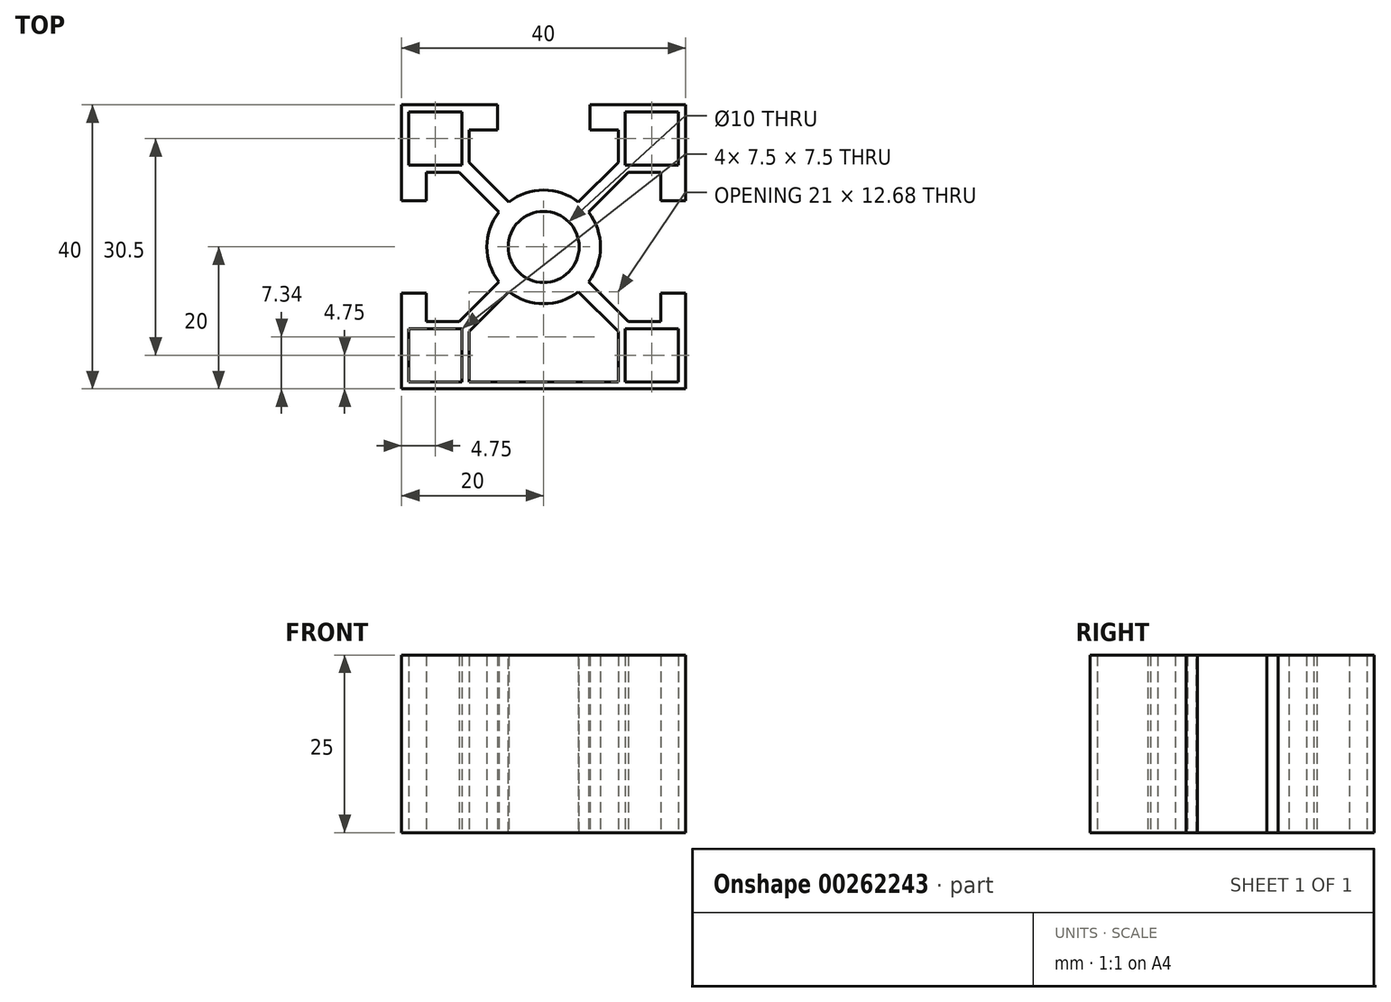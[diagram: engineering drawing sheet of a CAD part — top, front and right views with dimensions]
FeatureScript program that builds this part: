
annotation { "Feature Type Name" : "Feature", "Feature Type Description" : "" }
export const myFeature = defineFeature(function(context is Context, id is Id, definition is map)
    precondition{}
    {
        {
            var Q0;
            Q0=qCreatedBy(makeId("Top.planeOp"),FACE);
            var sketch = newSketch(context, id + "F0", { "sketchPlane" : qUnion([Q0])});
            skLineSegment(sketch, "E0.top", {"start": v(20, 20) * mm, "end": v(6.5, 20) * mm});
            skLineSegment(sketch, "E1.0", {"start": v(10.5, 16.5) * mm, "end": v(6.5, 16.5) * mm});
            skLineSegment(sketch, "E2.0", {"start": v(16.5, 6.5) * mm, "end": v(20, 6.5) * mm});
            skLineSegment(sketch, "E3", {"start": v(20, 20) * mm, "end": v(-20, -20) * mm, "construction": true});
            skLineSegment(sketch, "E4.MirrorCS", {"start": v(6.5, 16.5) * mm, "end": v(6.5, 20) * mm});
            skLineSegment(sketch, "E5.0", {"start": v(10.5, 11.91) * mm, "end": v(4.9, 6.32) * mm});
            skLineSegment(sketch, "E6.0", {"start": v(11.91, 10.5) * mm, "end": v(6.32, 4.9) * mm});
            skLineSegment(sketch, "E7.trimOffspring", {"start": v(20, 6.5) * mm, "end": v(20, 20) * mm});
            skLineSegment(sketch, "E8.trimOffspring", {"start": v(16.5, 6.5) * mm, "end": v(16.5, 10.5) * mm});
            skLineSegment(sketch, "E9", {"start": v(50.26, 0) * mm, "end": v(-51.39, 0) * mm, "construction": true});
            skLineSegment(sketch, "E10.0", {"start": v(10.5, 11.91) * mm, "end": v(10.5, 16.5) * mm});
            skLineSegment(sketch, "E10.1", {"start": v(11.91, 10.5) * mm, "end": v(16.5, 10.5) * mm});
            skLineSegment(sketch, "E11.0", {"start": v(19, 19) * mm, "end": v(11.5, 19) * mm});
            skLineSegment(sketch, "E11.1", {"start": v(19, 11.5) * mm, "end": v(19, 19) * mm});
            skLineSegment(sketch, "E12.0", {"start": v(11.5, 11.5) * mm, "end": v(19, 11.5) * mm});
            skLineSegment(sketch, "E12.1", {"start": v(11.5, 11.5) * mm, "end": v(11.5, 19) * mm});
            skArc(sketch, "E13", {"start": v(8, 0) * mm, "mid": v(7.57, 2.6) * mm, "end": v(6.32, 4.9) * mm});
            skLineSegment(sketch, "E14", {"start": v(0, 38.95) * mm, "end": v(0, -36.56) * mm, "construction": true});
            skArc(sketch, "E15.trimOffspring", {"start": v(4.9, 6.32) * mm, "mid": v(2.6, 7.57) * mm, "end": v(0, 8) * mm});
            skLineSegment(sketch, "E16.MirrorCS", {"start": v(-10.5, 16.5) * mm, "end": v(-6.5, 16.5) * mm});
            skArc(sketch, "E17.MirrorCS", {"start": v(-8, 0) * mm, "mid": v(-7.57, 2.6) * mm, "end": v(-6.32, 4.9) * mm});
            skLineSegment(sketch, "E18.MirrorCS", {"start": v(-11.5, 11.5) * mm, "end": v(-19, 11.5) * mm});
            skLineSegment(sketch, "E19.MirrorCS", {"start": v(-20, 20) * mm, "end": v(-6.5, 20) * mm});
            skLineSegment(sketch, "E20.MirrorCS", {"start": v(-19, 11.5) * mm, "end": v(-19, 19) * mm});
            skLineSegment(sketch, "E21.MirrorCS", {"start": v(-10.5, 11.91) * mm, "end": v(-10.5, 16.5) * mm});
            skLineSegment(sketch, "E22.MirrorCS", {"start": v(-10.5, 11.91) * mm, "end": v(-4.9, 6.32) * mm});
            skLineSegment(sketch, "E23.MirrorCS", {"start": v(-11.5, 11.5) * mm, "end": v(-11.5, 19) * mm});
            skLineSegment(sketch, "E24.MirrorCS", {"start": v(-16.5, 6.5) * mm, "end": v(-16.5, 10.5) * mm});
            skLineSegment(sketch, "E25.MirrorCS", {"start": v(-11.91, 10.5) * mm, "end": v(-16.5, 10.5) * mm});
            skLineSegment(sketch, "E26.MirrorCS", {"start": v(-19, 19) * mm, "end": v(-11.5, 19) * mm});
            skArc(sketch, "E27.MirrorCS", {"start": v(-4.9, 6.32) * mm, "mid": v(-2.6, 7.57) * mm, "end": v(0, 8) * mm});
            skLineSegment(sketch, "E28.MirrorCS", {"start": v(-6.5, 16.5) * mm, "end": v(-6.5, 20) * mm});
            skLineSegment(sketch, "E29.MirrorCS", {"start": v(-11.91, 10.5) * mm, "end": v(-6.32, 4.9) * mm});
            skLineSegment(sketch, "E30.MirrorCS", {"start": v(-20, 6.5) * mm, "end": v(-20, 20) * mm});
            skLineSegment(sketch, "E31.MirrorCS", {"start": v(-16.5, 6.5) * mm, "end": v(-20, 6.5) * mm});
            skLineSegment(sketch, "E32.MirrorCS", {"start": v(10.5, -11.91) * mm, "end": v(4.9, -6.32) * mm});
            skLineSegment(sketch, "E33.MirrorCS", {"start": v(10.5, -11.91) * mm, "end": v(10.5, -19) * mm});
            skLineSegment(sketch, "E34.MirrorCS", {"start": v(16.5, -6.5) * mm, "end": v(20, -6.5) * mm});
            skLineSegment(sketch, "E35.MirrorCS", {"start": v(-10.5, -11.91) * mm, "end": v(-4.9, -6.32) * mm});
            skLineSegment(sketch, "E36.MirrorCS", {"start": v(-11.91, -10.5) * mm, "end": v(-6.32, -4.9) * mm});
            skArc(sketch, "E37.MirrorCS", {"start": v(4.9, -6.32) * mm, "mid": v(2.6, -7.57) * mm, "end": v(0, -8) * mm});
            skArc(sketch, "E38.MirrorCS", {"start": v(8, 0) * mm, "mid": v(7.57, -2.6) * mm, "end": v(6.32, -4.9) * mm});
            skLineSegment(sketch, "E39.MirrorCS", {"start": v(-19, -19) * mm, "end": v(-11.5, -19) * mm});
            skLineSegment(sketch, "E40.MirrorCS", {"start": v(-20, -6.5) * mm, "end": v(-20, -20) * mm});
            skLineSegment(sketch, "E41.MirrorCS", {"start": v(-16.5, -6.5) * mm, "end": v(-20, -6.5) * mm});
            skArc(sketch, "E42.MirrorCS", {"start": v(-8, 0) * mm, "mid": v(-7.57, -2.6) * mm, "end": v(-6.32, -4.9) * mm});
            skLineSegment(sketch, "E43.MirrorCS", {"start": v(19, -19) * mm, "end": v(11.5, -19) * mm});
            skLineSegment(sketch, "E44.MirrorCS", {"start": v(11.5, -11.5) * mm, "end": v(11.5, -19) * mm});
            skLineSegment(sketch, "E45.MirrorCS", {"start": v(16.5, -6.5) * mm, "end": v(16.5, -10.5) * mm});
            skArc(sketch, "E46.MirrorCS", {"start": v(-4.9, -6.32) * mm, "mid": v(-2.6, -7.57) * mm, "end": v(0, -8) * mm});
            skLineSegment(sketch, "E47.MirrorCS", {"start": v(-16.5, -6.5) * mm, "end": v(-16.5, -10.5) * mm});
            skLineSegment(sketch, "E48.MirrorCS", {"start": v(-10.5, -11.91) * mm, "end": v(-10.5, -19) * mm});
            skLineSegment(sketch, "E49.MirrorCS", {"start": v(11.91, -10.5) * mm, "end": v(6.32, -4.9) * mm});
            skLineSegment(sketch, "E50.MirrorCS", {"start": v(19, -11.5) * mm, "end": v(19, -19) * mm});
            skLineSegment(sketch, "E51.MirrorCS", {"start": v(20, -6.5) * mm, "end": v(20, -20) * mm});
            skLineSegment(sketch, "E52.MirrorCS", {"start": v(-11.5, -11.5) * mm, "end": v(-19, -11.5) * mm});
            skLineSegment(sketch, "E53.MirrorCS", {"start": v(-20, -20) * mm, "end": v(20, -20) * mm});
            skLineSegment(sketch, "E54.MirrorCS", {"start": v(11.5, -11.5) * mm, "end": v(19, -11.5) * mm});
            skLineSegment(sketch, "E55.MirrorCS", {"start": v(-11.5, -11.5) * mm, "end": v(-11.5, -19) * mm});
            skLineSegment(sketch, "E56.MirrorCS", {"start": v(-11.91, -10.5) * mm, "end": v(-16.5, -10.5) * mm});
            skLineSegment(sketch, "E57.MirrorCS", {"start": v(11.91, -10.5) * mm, "end": v(16.5, -10.5) * mm});
            skLineSegment(sketch, "E58.MirrorCS", {"start": v(-19, -11.5) * mm, "end": v(-19, -19) * mm});
            skLineSegment(sketch, "E59", {"start": v(-10.5, -19) * mm, "end": v(10.5, -19) * mm});
            skSolve(sketch);
        }
        {
            var Q0;
            Q0=makeQuery(id+"F0.imprint","IMPRINT",FACE,{"disambiguationData":[TD([[makeQuery(id+"F0.imprint","IMPRINT",EDGE,{"derivedFrom":sQuery(id+"F0.wireOp",EDGE,"E0.top")}),1.0]])]});
            extrude(context, id + "F1", {"entities" : qUnion([Q0]), "depth" : 25 * mm});
        }
        {
            var Q0;
            Q0=makeQuery(id+"F1.opExtrude","CAP_FACE",FACE,{"disambiguationData":[OSD([sQuery(id+"F0.wireOp",EDGE,"E0.top"),sQuery(id+"F0.wireOp",EDGE,"E1.0"),sQuery(id+"F0.wireOp",EDGE,"E2.0"),sQuery(id+"F0.wireOp",EDGE,"E4.MirrorCS"),sQuery(id+"F0.wireOp",EDGE,"E5.0"),sQuery(id+"F0.wireOp",EDGE,"E6.0"),sQuery(id+"F0.wireOp",EDGE,"E7.trimOffspring"),sQuery(id+"F0.wireOp",EDGE,"E8.trimOffspring"),sQuery(id+"F0.wireOp",EDGE,"E10.0"),sQuery(id+"F0.wireOp",EDGE,"E10.1"),sQuery(id+"F0.wireOp",EDGE,"E11.0"),sQuery(id+"F0.wireOp",EDGE,"E11.1"),sQuery(id+"F0.wireOp",EDGE,"E12.0"),sQuery(id+"F0.wireOp",EDGE,"E12.1"),sQuery(id+"F0.wireOp",EDGE,"E13"),sQuery(id+"F0.wireOp",EDGE,"E15.trimOffspring"),sQuery(id+"F0.wireOp",EDGE,"E16.MirrorCS"),sQuery(id+"F0.wireOp",EDGE,"E17.MirrorCS"),sQuery(id+"F0.wireOp",EDGE,"E18.MirrorCS"),sQuery(id+"F0.wireOp",EDGE,"E20.MirrorCS"),sQuery(id+"F0.wireOp",EDGE,"E21.MirrorCS"),sQuery(id+"F0.wireOp",EDGE,"E22.MirrorCS"),sQuery(id+"F0.wireOp",EDGE,"E23.MirrorCS"),sQuery(id+"F0.wireOp",EDGE,"E24.MirrorCS"),sQuery(id+"F0.wireOp",EDGE,"E25.MirrorCS"),sQuery(id+"F0.wireOp",EDGE,"E26.MirrorCS"),sQuery(id+"F0.wireOp",EDGE,"E27.MirrorCS"),sQuery(id+"F0.wireOp",EDGE,"E29.MirrorCS"),sQuery(id+"F0.wireOp",EDGE,"E30.MirrorCS"),sQuery(id+"F0.wireOp",EDGE,"E31.MirrorCS"),sQuery(id+"F0.wireOp",EDGE,"E32.MirrorCS"),sQuery(id+"F0.wireOp",EDGE,"E33.MirrorCS"),sQuery(id+"F0.wireOp",EDGE,"E34.MirrorCS"),sQuery(id+"F0.wireOp",EDGE,"E35.MirrorCS"),sQuery(id+"F0.wireOp",EDGE,"E36.MirrorCS"),sQuery(id+"F0.wireOp",EDGE,"E37.MirrorCS"),sQuery(id+"F0.wireOp",EDGE,"E38.MirrorCS"),sQuery(id+"F0.wireOp",EDGE,"E39.MirrorCS"),sQuery(id+"F0.wireOp",EDGE,"E40.MirrorCS"),sQuery(id+"F0.wireOp",EDGE,"E41.MirrorCS"),sQuery(id+"F0.wireOp",EDGE,"E42.MirrorCS"),sQuery(id+"F0.wireOp",EDGE,"E43.MirrorCS"),sQuery(id+"F0.wireOp",EDGE,"E44.MirrorCS"),sQuery(id+"F0.wireOp",EDGE,"E45.MirrorCS"),sQuery(id+"F0.wireOp",EDGE,"E46.MirrorCS"),sQuery(id+"F0.wireOp",EDGE,"E47.MirrorCS"),sQuery(id+"F0.wireOp",EDGE,"E48.MirrorCS"),sQuery(id+"F0.wireOp",EDGE,"E49.MirrorCS"),sQuery(id+"F0.wireOp",EDGE,"E50.MirrorCS"),sQuery(id+"F0.wireOp",EDGE,"E51.MirrorCS"),sQuery(id+"F0.wireOp",EDGE,"E52.MirrorCS"),sQuery(id+"F0.wireOp",EDGE,"E53.MirrorCS"),sQuery(id+"F0.wireOp",EDGE,"E54.MirrorCS"),sQuery(id+"F0.wireOp",EDGE,"E55.MirrorCS"),sQuery(id+"F0.wireOp",EDGE,"E56.MirrorCS"),sQuery(id+"F0.wireOp",EDGE,"E57.MirrorCS"),sQuery(id+"F0.wireOp",EDGE,"E58.MirrorCS"),sQuery(id+"F0.wireOp",EDGE,"E19.MirrorCS"),sQuery(id+"F0.wireOp",EDGE,"E28.MirrorCS"),sQuery(id+"F0.wireOp",EDGE,"E59")])],"isStart":false});
            var sketch = newSketch(context, id + "F2", { "sketchPlane" : qUnion([Q0])});
            skCircle(sketch, "E60", {"center": v(0, 0) * mm, "radius": 5 * mm});
            skSolve(sketch);
        }
        {
            var Q0;
            Q0 = qSketchRegion(id + "F2", true);
            extrude(context, id + "F3", {"entities" : qUnion([Q0]), "operationType" : NewBodyOperationType.REMOVE, "endBound" : BoundingType.THROUGH_ALL, "oppositeDirection" : true, "depth" : 25 * mm});
        }
    });
